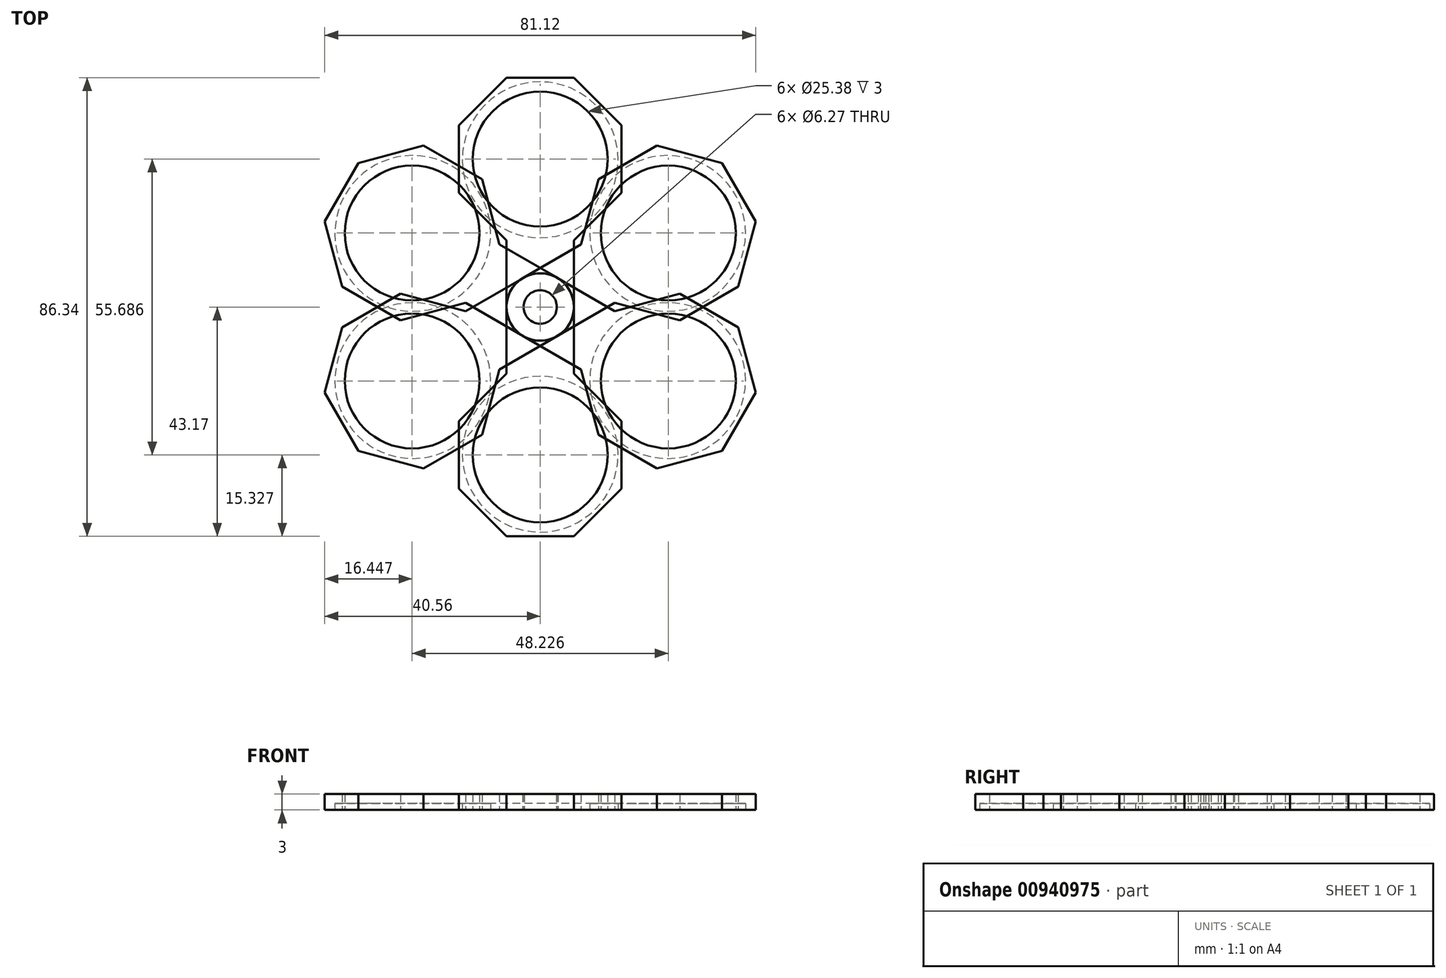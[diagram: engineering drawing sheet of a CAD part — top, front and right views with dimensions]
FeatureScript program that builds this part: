
annotation { "Feature Type Name" : "Feature", "Feature Type Description" : "" }
export const myFeature = defineFeature(function(context is Context, id is Id, definition is map)
    precondition{}
    {
        {
            var Q0;
            Q0=qCreatedBy(makeId("Right.planeOp"),FACE);
            var sketch = newSketch(context, id + "F0", { "sketchPlane" : qUnion([Q0])});
            skLineSegment(sketch, "E0", {"start": v(0, 0) * mm, "end": v(0, -30.73) * mm});
            skSolve(sketch);
        }
        {
            var Q0;
            Q0=qCreatedBy(makeId("Top.planeOp"),FACE);
            var sketch = newSketch(context, id + "F1", { "sketchPlane" : qUnion([Q0])});
            skCircle(sketch, "E1", {"center": v(0, 0) * mm, "radius": 3.14 * mm});
            skArc(sketch, "E2", {"start": v(-6.35, 0) * mm, "mid": v(0.09, -6.35) * mm, "end": v(6.35, 0.18) * mm});
            skLineSegment(sketch, "E3", {"start": v(0, 0) * mm, "end": v(0, 27.84) * mm, "construction": true});
            skLineSegment(sketch, "E4", {"start": v(6.35, -0.18) * mm, "end": v(6.35, 12.52) * mm});
            skLineSegment(sketch, "E5", {"start": v(-6.35, 12.52) * mm, "end": v(-6.35, 0) * mm});
            skCircle(sketch, "E6", {"center": v(0, 27.84) * mm, "radius": 12.7 * mm});
            skCircle(sketch, "E7.cCircle", {"center": v(0, 27.84) * mm, "radius": 15.32 * mm, "construction": true});
            skLineSegment(sketch, "E7.0", {"start": v(15.32, 34.2) * mm, "end": v(15.32, 21.5) * mm});
            skLineSegment(sketch, "E7.1", {"start": v(15.32, 21.5) * mm, "end": v(6.35, 12.52) * mm});
            skLineSegment(sketch, "E7.2", {"start": v(6.35, 12.52) * mm, "end": v(-6.35, 12.52) * mm, "construction": true});
            skLineSegment(sketch, "E7.3", {"start": v(-6.35, 12.52) * mm, "end": v(-15.32, 21.5) * mm});
            skLineSegment(sketch, "E7.4", {"start": v(-15.32, 21.5) * mm, "end": v(-15.32, 34.2) * mm});
            skLineSegment(sketch, "E7.5", {"start": v(-15.32, 34.2) * mm, "end": v(-6.35, 43.17) * mm});
            skLineSegment(sketch, "E7.6", {"start": v(-6.35, 43.17) * mm, "end": v(6.35, 43.17) * mm});
            skLineSegment(sketch, "E7.7", {"start": v(6.35, 43.17) * mm, "end": v(15.32, 34.2) * mm});
            skPoint(sketch, "E7.0.midPoint", {"position": v(15.32, 27.84) * mm});
            skSolve(sketch);
        }
        {
            var Q0;
            {var subQ0=sQuery(id+"F1.wireOp",EDGE,"E4");Q0=makeQuery(id+"F1.imprint","IMPRINT",FACE,{"disambiguationData":[TD([[makeQuery(id+"F1.imprint","IMPRINT",EDGE,{"derivedFrom":subQ0}),1.0]])]});}
            var Q1;
            Q1=makeQuery(id+"F1.imprint","IMPRINT",FACE,{"disambiguationData":[TD([[makeQuery(id+"F1.imprint","IMPRINT",EDGE,{"derivedFrom":sQuery(id+"F1.wireOp",EDGE,"E1")}),-1.0]])]});
            var Q2;
            {var subQ0=sQuery(id+"F1.wireOp",EDGE,"E5");Q2=makeQuery(id+"F1.imprint","IMPRINT",FACE,{"disambiguationData":[TD([[makeQuery(id+"F1.imprint","IMPRINT",EDGE,{"derivedFrom":subQ0}),1.0]])]});}
            var Q3;
            Q3=makeQuery(id+"F1.imprint","IMPRINT",FACE,{"disambiguationData":[TD([[makeQuery(id+"F1.imprint","IMPRINT",EDGE,{"derivedFrom":sQuery(id+"F1.wireOp",EDGE,"E1")}),1.0]])]});
            var Q4;
            {var subQ3=sQuery(id+"F1.wireOp",EDGE,"dbdc143a-07b7-4892-8d22-ca39ddf19d05.0");Q4=makeQuery(id+"F1.imprint","IMPRINT",FACE,{"disambiguationData":[TD([[makeQuery(id+"F1.imprint","IMPRINT",EDGE,{"derivedFrom":subQ3}),-1.0]])]});}
            var Q5;
            Q5=makeQuery(id+"F1.imprint","IMPRINT",FACE,{"disambiguationData":[TD([[makeQuery(id+"F1.imprint","IMPRINT",EDGE,{"derivedFrom":sQuery(id+"F1.wireOp",EDGE,"E6")}),-1.0]])]});
            extrude(context, id + "F2", {"entities" : qUnion([Q0, Q1, Q2, Q3, Q4, Q5]), "depth" : 3 * mm, "offsetDistance" : 25.4 * mm});
        }
        {
            var Q0;
            Q0=makeQuery(id+"F2.opExtrude","SWEPT_BODY",BODY,{"disambiguationData":[OSD([sQuery(id+"F1.wireOp",EDGE,"E2"),sQuery(id+"F1.wireOp",EDGE,"E4"),sQuery(id+"F1.wireOp",EDGE,"dbdc143a-07b7-4892-8d22-ca39ddf19d05.0"),sQuery(id+"F1.wireOp",EDGE,"dbdc143a-07b7-4892-8d22-ca39ddf19d05.2"),sQuery(id+"F1.wireOp",EDGE,"dbdc143a-07b7-4892-8d22-ca39ddf19d05.3"),sQuery(id+"F1.wireOp",EDGE,"dbdc143a-07b7-4892-8d22-ca39ddf19d05.4"),sQuery(id+"F1.wireOp",EDGE,"dbdc143a-07b7-4892-8d22-ca39ddf19d05.5"),sQuery(id+"F1.wireOp",EDGE,"dbdc143a-07b7-4892-8d22-ca39ddf19d05.6"),sQuery(id+"F1.wireOp",EDGE,"E5"),sQuery(id+"F1.wireOp",EDGE,"E6"),sQuery(id+"F1.wireOp",EDGE,"ee19e062-d455-4960-8eef-03f5539e37c2.0"),sQuery(id+"F1.wireOp",EDGE,"ee19e062-d455-4960-8eef-03f5539e37c2.2"),sQuery(id+"F1.wireOp",EDGE,"ee19e062-d455-4960-8eef-03f5539e37c2.4"),sQuery(id+"F1.wireOp",EDGE,"ee19e062-d455-4960-8eef-03f5539e37c2.5"),sQuery(id+"F1.wireOp",EDGE,"7a236b8d-d41c-4182-b9e4-392b86f8f832.3"),sQuery(id+"F1.wireOp",EDGE,"7a236b8d-d41c-4182-b9e4-392b86f8f832.4"),sQuery(id+"F1.wireOp",EDGE,"7a236b8d-d41c-4182-b9e4-392b86f8f832.5"),sQuery(id+"F1.wireOp",EDGE,"OZb6LWr4-ic3p-ZZsX-V20N-EMgBvSCYZ7qY"),sQuery(id+"F1.wireOp",EDGE,"41ASrNWs-cKd8-D1L3-PlCW-tTzetjR4aqx4"),sQuery(id+"F1.wireOp",EDGE,"VU6zZ8PQ-uMKg-Zo6W-pWSG-ATd19DIpABhN"),sQuery(id+"F1.wireOp",EDGE,"R1gD17Gi-Qkg9-vewI-2wWV-GJsHAJTkMCUr"),sQuery(id+"F1.wireOp",EDGE,"RJGgUM2Y-PClg-Gihj-KSs4-uw2COGgmtFFU"),sQuery(id+"F1.wireOp",EDGE,"c38snv5j-GRH1-zRro-A039-Qwm5epmKFArT"),sQuery(id+"F1.wireOp",EDGE,"cWRG6j9r-rlyd-stQu-ReQ0-OGvMunmdC53s"),sQuery(id+"F1.wireOp",EDGE,"OIqEnAyR-bgmS-pgzN-3YcM-9qaxklVizTed")])]});
            var Q1;
            Q1=sQuery(id+"F0.wireOp",EDGE,"E0");
            circularPattern(context, id + "F3", {"entities" : qUnion([Q0]), "axis" : qUnion([Q1]), "angle" : 360 * degree, "instanceCount" : 6, "equalSpace" : true});
        }
        {
            var Q0;
            Q0=qCreatedBy(makeId("Front.planeOp"),FACE);
            var sketch = newSketch(context, id + "F4", { "sketchPlane" : qUnion([Q0])});
            skLineSegment(sketch, "E8", {"start": v(0, 0) * mm, "end": v(0, -22.1) * mm});
            skSolve(sketch);
        }
        {
            var Q0;
            Q0=qCreatedBy(makeId("Top.planeOp"),FACE);
            var sketch = newSketch(context, id + "F5", { "sketchPlane" : qUnion([Q0])});
            skCircle(sketch, "E9", {"center": v(0, 27.7) * mm, "radius": 14.67 * mm});
            skSolve(sketch);
        }
        {
            var Q0;
            Q0 = qSketchRegion(id + "F5", true);
            extrude(context, id + "F6", {"entities" : qUnion([Q0]), "depth" : 1.2 * mm, "offsetDistance" : 25.4 * mm});
        }
        {
            var Q0;
            Q0=makeQuery(id+"F6.opExtrude","SWEPT_BODY",BODY,{"disambiguationData":[OSD([sQuery(id+"F5.wireOp",EDGE,"E9")])]});
            var Q1;
            Q1=sQuery(id+"F4.wireOp",EDGE,"E8");
            circularPattern(context, id + "F7", {"entities" : qUnion([Q0]), "axis" : qUnion([Q1]), "angle" : 360 * degree, "instanceCount" : 6, "equalSpace" : true});
        }
        {
            var Q0;
            Q0=qCreatedBy(makeId("Top.planeOp"),FACE);
            var sketch = newSketch(context, id + "F8", { "sketchPlane" : qUnion([Q0])});
            skCircle(sketch, "E10", {"center": v(0, 0) * mm, "radius": 3.14 * mm});
            skSolve(sketch);
        }
        {
            var Q0;
            Q0=makeQuery(id+"F8.imprint","IMPRINT",FACE,{"disambiguationData":[TD([[makeQuery(id+"F8.imprint","IMPRINT",EDGE,{"derivedFrom":sQuery(id+"F8.wireOp",EDGE,"E10")}),1.0]])]});
            extrude(context, id + "F9", {"entities" : qUnion([Q0]), "operationType" : NewBodyOperationType.REMOVE, "oppositeDirection" : true, "depth" : -25.4 * mm, "offsetDistance" : 25.4 * mm});
        }
    });
